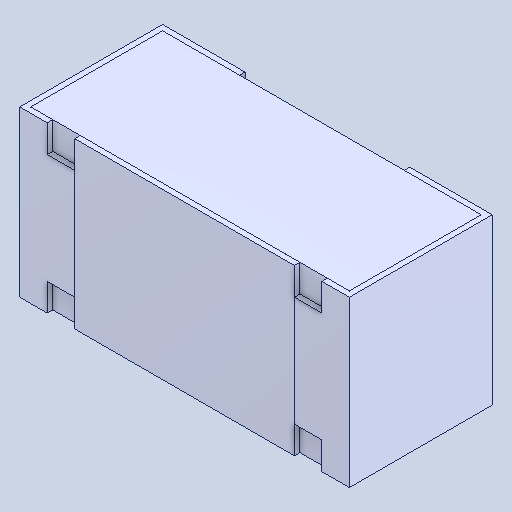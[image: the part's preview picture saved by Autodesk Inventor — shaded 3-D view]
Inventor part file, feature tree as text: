
AUTODESK INVENTOR PART (.ipt)
format: ipt  version: 2025 (Build 290162000, 162)  size: 113,664 bytes
history: native  units: mm
features: boolean_combine x2, other x1, mirror x1
ambient origin geometry x8: Origin, YZ Plane, XZ Plane, XY Plane, X Axis, Y Axis, Z Axis, Center Point
bodies: Solid1 (feature_tree), Solid2 (feature_tree), Solid3 (feature_tree), Solid4 (feature_tree)
feature tree (4):
  other  "Cut-Extrude1"
  boolean_combine  "Combine2"
  mirror  "Mirror1[3]"
  boolean_combine  "Combine1"
